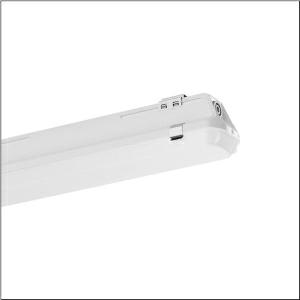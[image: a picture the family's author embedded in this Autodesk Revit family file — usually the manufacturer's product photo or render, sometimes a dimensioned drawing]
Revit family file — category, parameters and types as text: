
# Revit family: monsun_r__11_parking_51fg20dp440hhq_4cc6
name_source: partatom
category: Lighting Fixtures
units: mm (PartAtom-declared; Revit-internal decimal feet)

## family parameters
Cut with Voids When Loaded = No
Host = Face
Light Source = No
Part Type = Normal
Room Calculation Point = No
Round Connector Dimension = Use Diameter
Shared = No

## types (1)
- --- (1 x LED, 4840 lm, 31.3 W, 4000K)
    Apparent Load = 31 VA
    CIE Flux Codes = 45 75 93 94 100
    Color Rendering = 80
    Color Temperature = 4000K
    Default Elevation = 1800 mm
    Description = Monsun® 11 parking, damp-proof luminaire, chain hanger, primary optical cover: enclosure, of PC, light emission: direct distribution, primary light characteristic: symmetric, installation type: suspended mounting, surface-mounted, horizontal mounting, vertical mounting, LED, rated luminous flux: 4.840lm, luminous efficacy: 157lm/W, light colour: 840, colour temperature: 4000K, control gear: ECG DALI, with terminal, 5-pole, max. 2.5mm², mains connection: 220..240V, AC, 50/60Hz, rated input power: 31W, housing, of glass-fibre reinforced polyester, uncoated, bright grey, incl. chain hanger, length: 1.590mm, width: 90mm, height: 88mm, clip for enclosure, of stainless steel (V2A), ceiling mounting element, of stainless steel (V2A), chain hanger, of stainless steel (V2A), multi-sensor HC1, local controlcentral control, equipment: slave, scope of services: certified according to part 101,103,303,304, dimmable, protection rating (complete): IP66, insulation class (complete): insulation class I (protective earthing), certification: CE, ENEC, VDE, UKCA, protection symbol: D, impact resistance: IK08, permissible operating ambient temperature: -25..+40°C, standard: EN 50419, EN 60598-2-1, corresponds to IFS (International Featured Standards) requirements for safety and quality in the food industry, for indoor or canopied outdoor use, no direct snow, no direct sun, no direct rain, contact your sales advisor before using the luminaires in applications with unclear chemical exposure, large temperature fluctuations or condensation-forming humidity, LABS conformity tested according to VDMA 24364:2018-05, packaging unit: 1 piece
    Height = 89 mm
    Lamp = 1 x LED
    Lamp Light Flux = 4840 lm
    Lamp Power = 31.3 W
    Lamp count = 1
    Length = 1590 mm
    Luminous efficacy = 155 lm/W
    Manufacturer = Siteco
    ModVariant = No
    Model = 51FG20DP440HHQ
    Mounting Place = Ceiling
    Mounting Type = Surface mounted
    Number of Poles = 1
    OnlyDefault = Yes
    Power Factor = 1
    Product Name = Monsun® 11 parking
    Product group = damp-proof luminaire
    ProductGroupID = 300
    Protection Class = Protection class I
    Protection Degree = IP 66
    RLX_Detail_Level = 1
    RLX_Emergency_Light_Flux = 0 lm
    RLX_Emergency_Type = 0
    RLX_Emergency_Type_DB = No
    RlxData = <blob elided: 92137 chars, md5=ca58c893>
    Socket = socket
    Standby Power = 0 W
    System Light Flux = 4840 lm
    System Power = 31 W
    Type Comments = factory setting: luminous flux: 100 % | dim-lin: 254 | 205 mA
    Type Image = l_1004748.jpg
    URL = http://relux.com
    VarID = @adj_074711
    Voltage = 0 V
    Weight = 0.00 kg
    Width = 90 mm

## geometry (parser evidence)
native form markers: Blend x4, Sweep x15
no freeform markers — native parametric forms only
